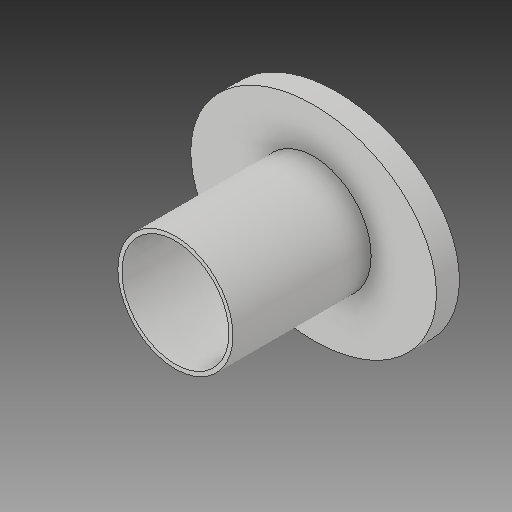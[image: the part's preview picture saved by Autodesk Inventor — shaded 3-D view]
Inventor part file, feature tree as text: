
AUTODESK INVENTOR PART (.ipt)
format: ipt  version: 2018 (Build 220112000, 112)  size: 120,832 bytes
history: native  units: mm
features: sketch x4, other x3
ambient origin geometry x8: Origin, YZ Plane, XZ Plane, XY Plane, X Axis, Y Axis, Z Axis, Center Point
bodies: Solid1 (feature_tree)
feature tree (7):
  other  "Pushfit-adapter-cap.ipt"
  other  "Solid1::Pushfit-adapter-cap.ipt"
  other  "TaggingFeature1"
  sketch  "Sketch1"  dims[d0=10.0mm]
  sketch  "Sketch2"
  sketch  "Sketch3"
  sketch  "Sketch4"
